# Revit family: FP-Revit20-en-EB30MSB3-BuiltInCoffeeMaker-0-90005525A-US-CA
name_source: partatom
category: Specialty Equipment
units: mm (PartAtom-declared; Revit-internal decimal feet)

## family parameters
Always vertical = Yes
Cut with Voids When Loaded = Yes
OmniClass Number = 23.40.40.14.17.31
OmniClass Title = Small Specialized Cooking Equipment
Part Type = Normal
Room Calculation Point = No
Round Connector Dimension = Use Diameter
Shared = No
Work Plane-Based = No

## types (1)
- EB30MSB3
    Cavity - Depth = 545 mm  [stored 1.78806 ft]
    Cavity - Height = 450 mm
    Cavity - Width = 560 mm  [stored 1.83727 ft]
    Connector Description - Electrical = 120 V, 60 Hz, 10A circuit
    Default Elevation = 0 mm  [stored 0 ft]
    Description = 30in Built-In Coffee Maker
    Manufacturer = Fisher & Paykel Appliances
    Material - Front = Fisher & Paykel - Glass, Black
    Material - Trim = Fisher & Paykel - Aluminium, Dark
    Model = EB30MSB3
    Opening - Depth = 20 mm  [stored 0.0656168 ft]
    Opening - Height = 460 mm  [stored 1.50919 ft]
    Opening - Width = 762 mm  [stored 2.5 ft]
    Type Comments = Minimal Black
    URL = www.fisherpaykel.com
    Visibility - 2 x 1mm spacers = Yes
    Visibility - Clearance Required = Yes

note: [stored X ft] marks values corroborated as IEEE doubles in the binary element streams (Revit-internal decimal feet)

## geometry (parser evidence)
native form markers: Sweep x10
no freeform markers — native parametric forms only
